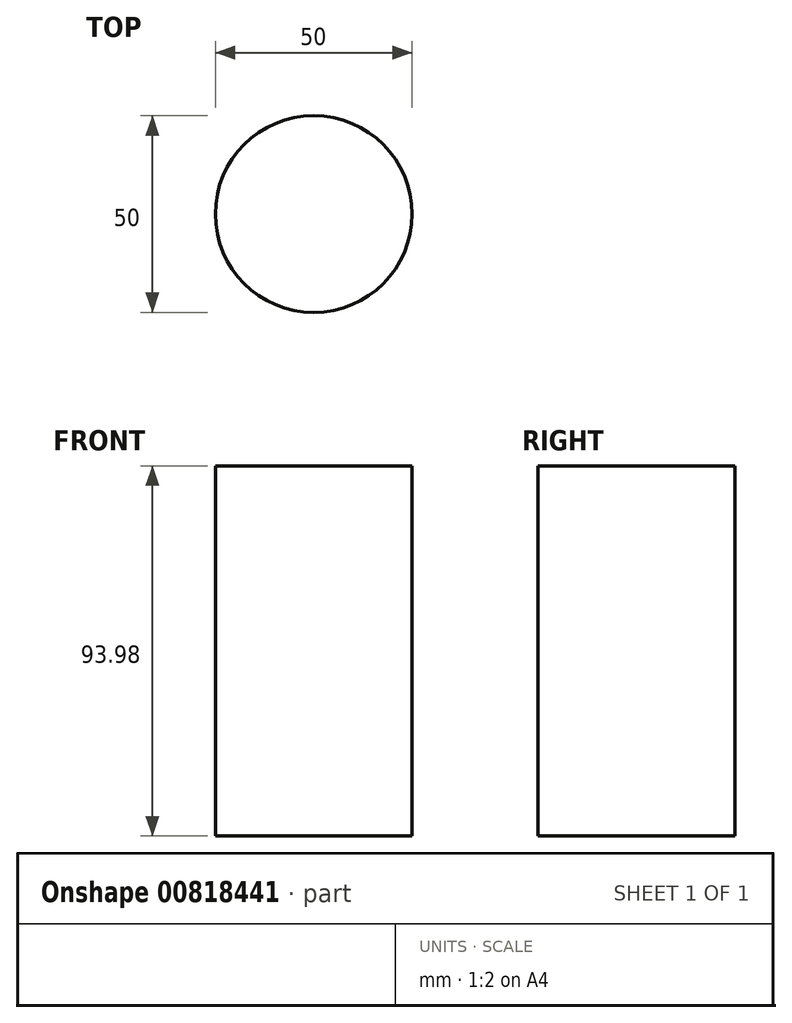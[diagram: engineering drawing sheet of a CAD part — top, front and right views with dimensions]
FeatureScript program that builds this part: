
annotation { "Feature Type Name" : "Feature", "Feature Type Description" : "" }
export const myFeature = defineFeature(function(context is Context, id is Id, definition is map)
    precondition{}
    {
        {
            var Q0;
            Q0=qCreatedBy(makeId("Top.planeOp"),FACE);
            var sketch = newSketch(context, id + "F0", { "sketchPlane" : qUnion([Q0])});
            skCircle(sketch, "E0", {"center": v(0, 0) * mm, "radius": 25 * mm});
            skSolve(sketch);
        }
        {
            var Q0;
            Q0=makeQuery(id+"F0.imprint","IMPRINT",FACE,{"disambiguationData":[TD([[makeQuery(id+"F0.imprint","IMPRINT",EDGE,{"derivedFrom":sQuery(id+"F0.wireOp",EDGE,"E0")}),1.0]])]});
            extrude(context, id + "F1", {"entities" : qUnion([Q0]), "depth" : 93.98 * mm, "offsetDistance" : 25.4 * mm});
        }
    });
